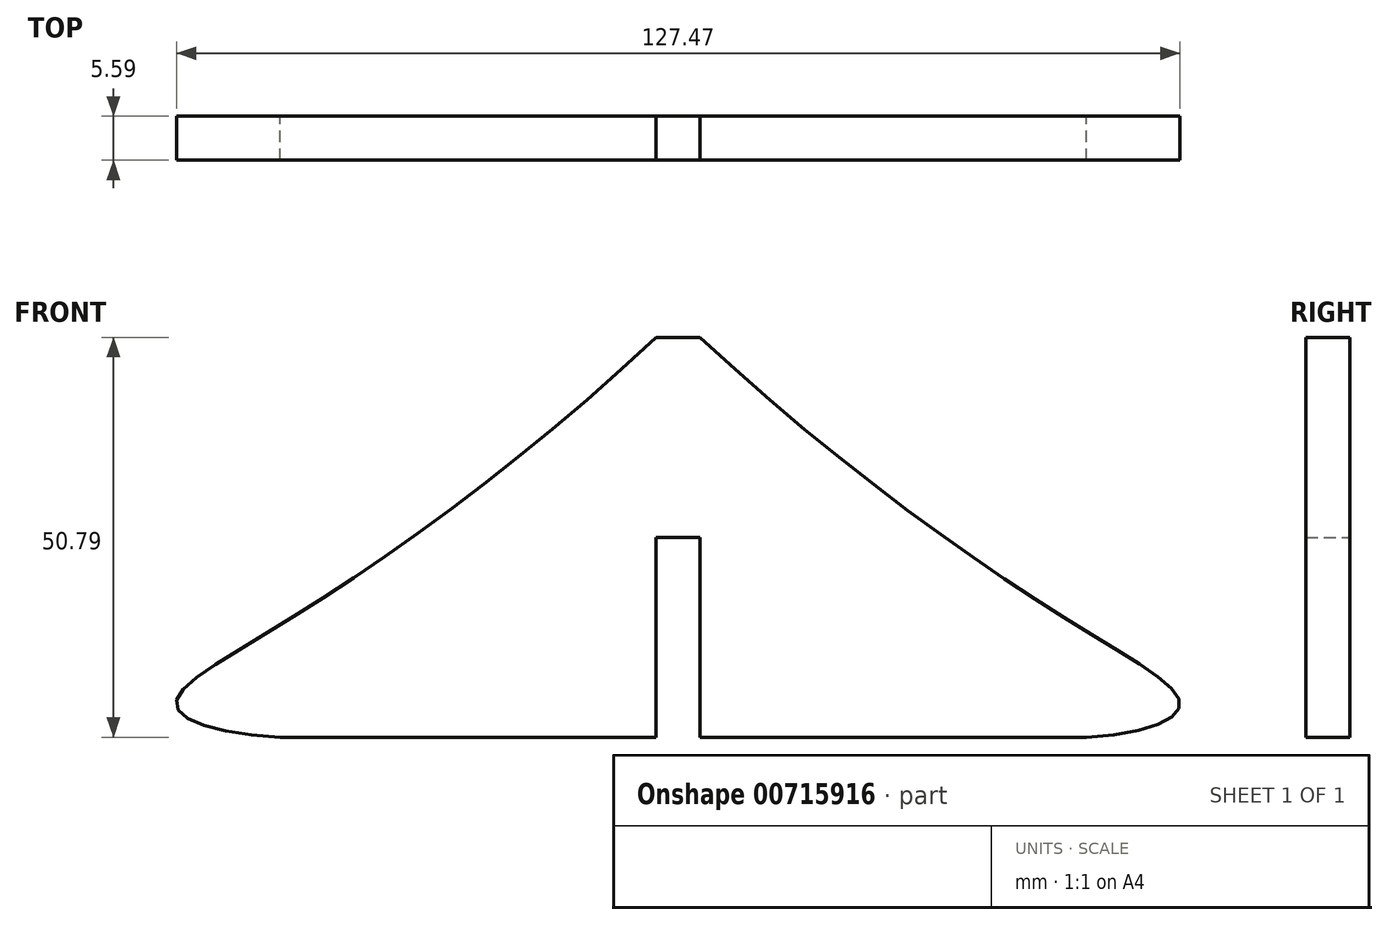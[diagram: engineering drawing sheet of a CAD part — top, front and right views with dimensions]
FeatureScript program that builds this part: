
annotation { "Feature Type Name" : "Feature", "Feature Type Description" : "" }
export const myFeature = defineFeature(function(context is Context, id is Id, definition is map)
    precondition{}
    {
        {
            var Q0;
            Q0=qCreatedBy(makeId("Front.planeOp"),FACE);
            var sketch = newSketch(context, id + "F0", { "sketchPlane" : qUnion([Q0])});
            skLineSegment(sketch, "E0.bottom", {"start": v(0, 0) * mm, "end": v(381, 0) * mm});
            skLineSegment(sketch, "E0.top", {"start": v(0, 298.45) * mm, "end": v(381, 298.45) * mm});
            skLineSegment(sketch, "E0.left", {"start": v(0, 0) * mm, "end": v(0, 298.45) * mm});
            skLineSegment(sketch, "E0.right", {"start": v(381, 0) * mm, "end": v(381, 298.45) * mm});
            skLineSegment(sketch, "E1", {"start": v(59.25, 135.98) * mm, "end": v(107.05, 135.98) * mm});
            skLineSegment(sketch, "E2", {"start": v(107.05, 161.38) * mm, "end": v(107.05, 135.98) * mm});
            skLineSegment(sketch, "E3", {"start": v(112.64, 161.38) * mm, "end": v(112.64, 135.98) * mm});
            skLineSegment(sketch, "E4", {"start": v(107.05, 161.38) * mm, "end": v(112.64, 161.38) * mm});
            skLineSegment(sketch, "E5.trimOffspring", {"start": v(112.64, 135.98) * mm, "end": v(163.44, 135.98) * mm});
            skLineSegment(sketch, "E6.top", {"start": v(107.05, 186.77) * mm, "end": v(112.64, 186.77) * mm});
            skFitSpline(sketch, "E7", {"points": [v(59.25, 135.98) * mm, v(46.12, 140.05) * mm, v(59.25, 150.22) * mm, v(107.05, 186.77) * mm], "startDerivative": vector(-85.67, 3.97) * mm, "endDerivative": vector(101, 94.65) * mm});
            skFitSpline(sketch, "E8.MirrorCS", {"points": [v(161.68, 135.98) * mm, v(173.56, 140.05) * mm, v(161.68, 149.42) * mm, v(112.64, 186.77) * mm], "startDerivative": vector(85.67, 3.97) * mm, "endDerivative": vector(-101, 94.65) * mm});
            skSolve(sketch);
        }
        {
            var Q0;
            Q0=makeQuery(id+"F0.imprint","IMPRINT",FACE,{"disambiguationData":[TD([[makeQuery(id+"F0.imprint","IMPRINT",EDGE,{"derivedFrom":sQuery(id+"F0.wireOp",EDGE,"E1")}),1.0]])]});
            extrude(context, id + "F1", {"entities" : qUnion([Q0]), "depth" : 5.6 * mm, "offsetDistance" : 25.4 * mm});
        }
    });
